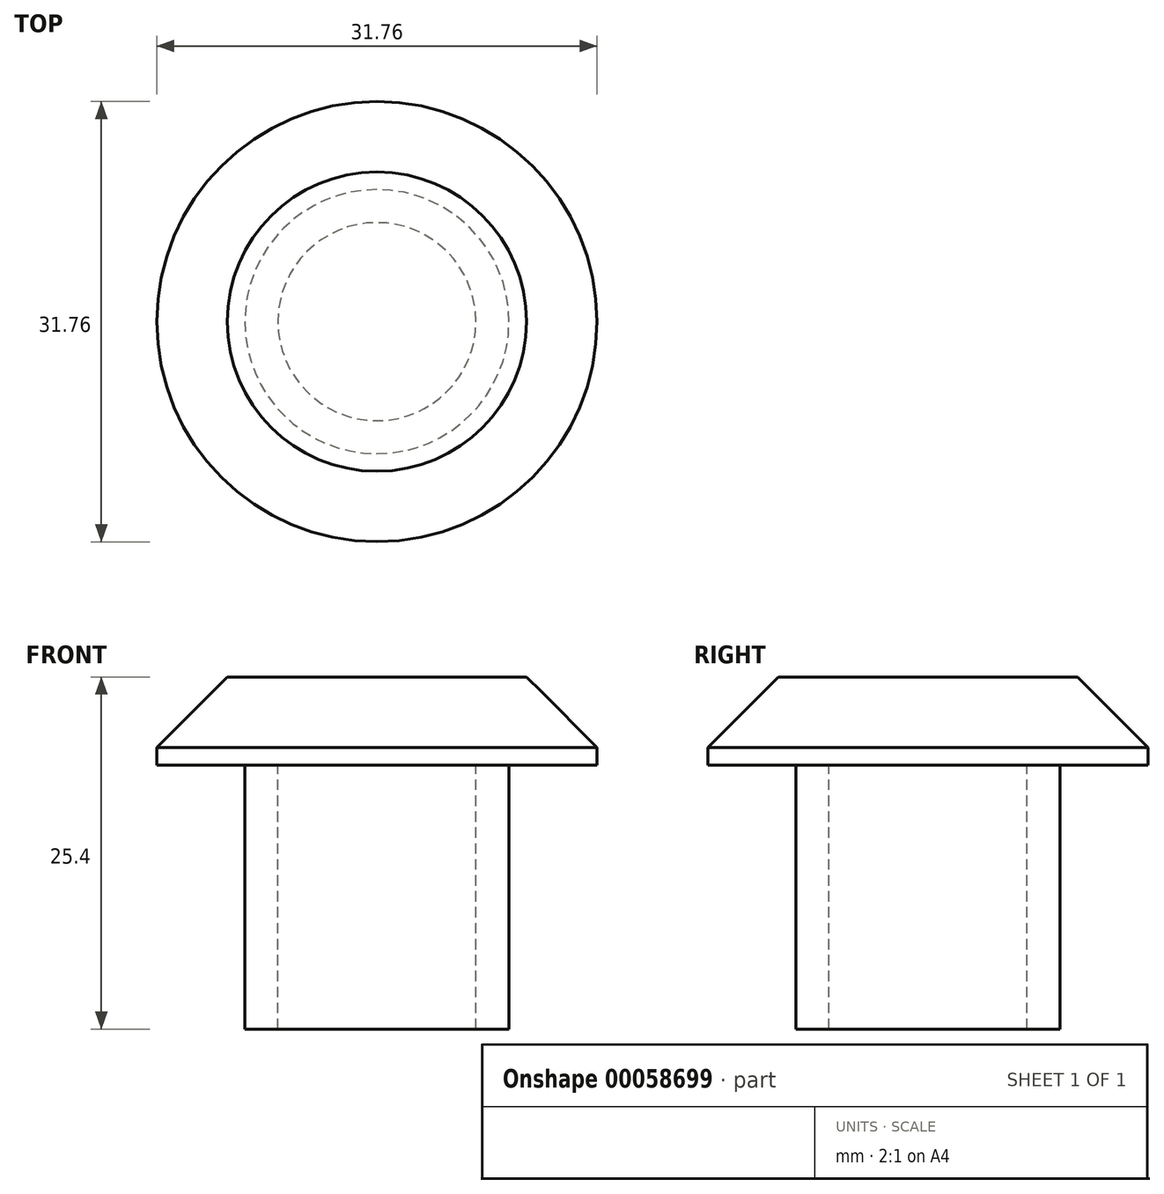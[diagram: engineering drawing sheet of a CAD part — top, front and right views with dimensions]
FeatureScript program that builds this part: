
annotation { "Feature Type Name" : "Feature", "Feature Type Description" : "" }
export const myFeature = defineFeature(function(context is Context, id is Id, definition is map)
    precondition{}
    {
        {
            var Q0;
            Q0=qCreatedBy(makeId("Top.planeOp"),FACE);
            var sketch = newSketch(context, id + "F0", { "sketchPlane" : qUnion([Q0])});
            skCircle(sketch, "E0", {"center": v(0, 0) * mm, "radius": 15.88 * mm});
            skSolve(sketch);
        }
        {
            var Q0;
            Q0=makeQuery(id+"F0.imprint","IMPRINT",FACE,{"disambiguationData":[TD([[makeQuery(id+"F0.imprint","IMPRINT",EDGE,{"derivedFrom":sQuery(id+"F0.wireOp",EDGE,"E0")}),1.0]])]});
            extrude(context, id + "F1", {"entities" : qUnion([Q0]), "depth" : 6.35 * mm});
        }
        {
            var Q0;
            Q0=makeQuery(id+"F1.opExtrude","CAP_FACE",FACE,{"disambiguationData":[OSD([sQuery(id+"F0.wireOp",EDGE,"E0")])],"isStart":false});
            chamfer(context, id + "F2", {"entities" : qUnion([Q0]), "width" : 5.08 * mm, "tangentPropagation" : true});
        }
        {
            var Q0;
            Q0=makeQuery(id+"F1.opExtrude","CAP_FACE",FACE,{"disambiguationData":[OSD([sQuery(id+"F0.wireOp",EDGE,"E0")])],"isStart":true});
            var sketch = newSketch(context, id + "F3", { "sketchPlane" : qUnion([Q0])});
            skCircle(sketch, "E1", {"center": v(0, 0) * mm, "radius": 7.14 * mm});
            skCircle(sketch, "E2", {"center": v(0, 0) * mm, "radius": 9.53 * mm});
            skSolve(sketch);
        }
        {
            var Q0;
            Q0=makeQuery(id+"F3.imprint","IMPRINT",FACE,{"disambiguationData":[TD([[makeQuery(id+"F3.imprint","IMPRINT",EDGE,{"derivedFrom":sQuery(id+"F3.wireOp",EDGE,"E1")}),-1.0]])]});
            extrude(context, id + "F4", {"entities" : qUnion([Q0]), "operationType" : NewBodyOperationType.ADD, "depth" : 19.05 * mm});
        }
    });
